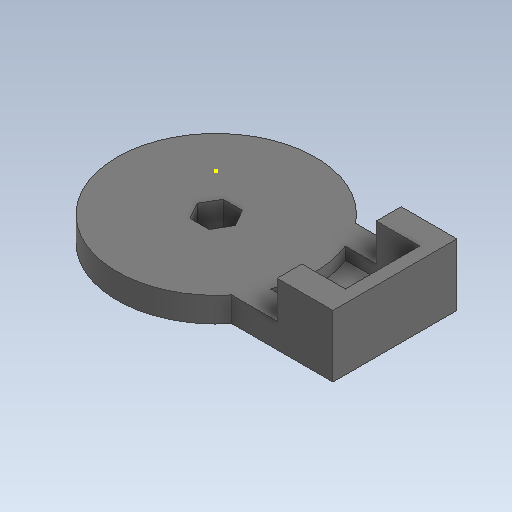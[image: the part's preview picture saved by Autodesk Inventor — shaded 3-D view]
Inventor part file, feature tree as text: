
AUTODESK INVENTOR PART (.ipt)
format: ipt  version: 2021.2 (Build 252289000, 289)  size: 187,904 bytes
history: native  units: in
note: dims shown in document units (in); Inventor stores cm internally (conversion verified against a paired STEP export)
features: sketch x7, extrude x6, other x2, revolve x1, mirror x1, reference x1
ambient origin geometry x8: Origin, YZ Plane, XZ Plane, XY Plane, X Axis, Y Axis, Z Axis, Center Point
bodies: Solid1 (feature_tree)
feature tree (18):
  revolve  "Revolution1"  [1 undecoded]
  extrude  "Extrusion1"  TaperAngle=90.0deg  [1 undecoded]
  extrude  "Extrusion3"  Depth=0.9in
  extrude  "Extrusion4"  Depth=0.5in TaperAngle=0.0deg
  extrude  "Extrusion5"  Depth=0.5in
  mirror  "Mirror1"
  extrude  "Extrusion6"  Depth=0.5in TaperAngle=0.0deg
  extrude  "Extrusion7"  Depth=0.75in TaperAngle=0.0deg
  sketch  "Sketch12"  dims[d28=0.875in d29=0.75in d30=0.0in d31=0.39in d32=0.0in d33=0.0in d34=0.25in d35=0.0in d36=0.25in d37=0.0in]
  sketch  "Sketch5"  dims[d0=2.0in d1=0.1969in]
  sketch  "Sketch7"  dims[d2=0.4751in d6=90.0deg]
  sketch  "Sketch8"  dims[d13=0.9in d15=1.24in]
  sketch  "Sketch9"  dims[d16=0.6693in d17=0.5in d18=0.0in]
  reference  "Reference1"
  sketch  "Sketch10"  dims[d23=1.5in d24=0.5in]
  sketch  "Sketch11"  dims[d25=0.75in d26=0.5in d27=0.0in]
  other  "ForkMountWithCelestronTubeConnector.iam"
  other  "6x3_8-keyedDriveShaft:2"
note: 2 required parameter values undecoded (feature->parameter linkage not recoverable at this tier; creation-order binding heuristic only, values carry confidence <= 0.55)